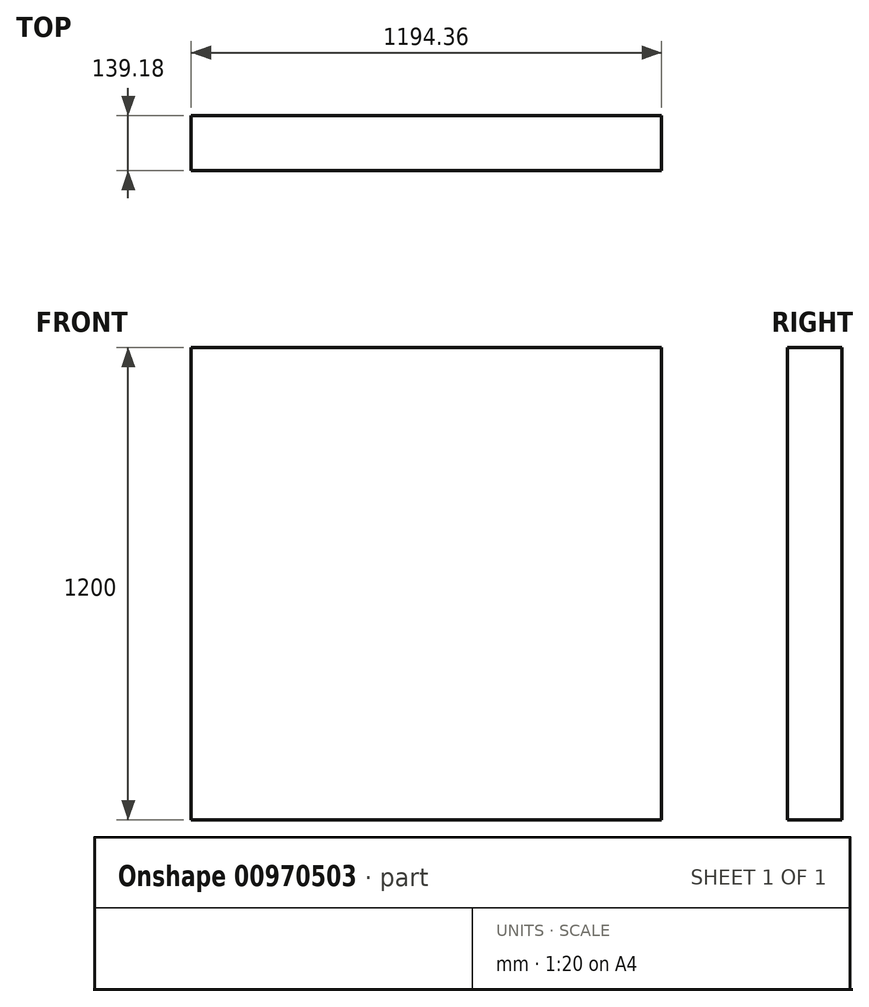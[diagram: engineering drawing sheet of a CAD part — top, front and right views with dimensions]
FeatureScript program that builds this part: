
annotation { "Feature Type Name" : "Feature", "Feature Type Description" : "" }
export const myFeature = defineFeature(function(context is Context, id is Id, definition is map)
    precondition{}
    {
        {
            var Q0;
            Q0=qCreatedBy(makeId("Top.planeOp"),FACE);
            var sketch = newSketch(context, id + "F0", { "sketchPlane" : qUnion([Q0])});
            skLineSegment(sketch, "E0.bottom", {"start": v(597.18, 69.6) * mm, "end": v(-597.18, 69.6) * mm});
            skLineSegment(sketch, "E0.top", {"start": v(597.18, -69.6) * mm, "end": v(-597.18, -69.6) * mm});
            skLineSegment(sketch, "E0.left", {"start": v(597.18, 69.6) * mm, "end": v(597.18, -69.6) * mm});
            skLineSegment(sketch, "E0.right", {"start": v(-597.18, 69.6) * mm, "end": v(-597.18, -69.6) * mm});
            skPoint(sketch, "E0.middle", {"position": v(0, 0) * mm});
            skSolve(sketch);
        }
        {
            var Q0;
            Q0=makeQuery(id+"F0.imprint","IMPRINT",FACE,{"disambiguationData":[TD([[makeQuery(id+"F0.imprint","IMPRINT",EDGE,{"derivedFrom":sQuery(id+"F0.wireOp",EDGE,"E0.bottom")}),1.0]])]});
            extrude(context, id + "F1", {"entities" : qUnion([Q0]), "depth" : 1200 * mm, "offsetDistance" : 25 * mm});
        }
    });
